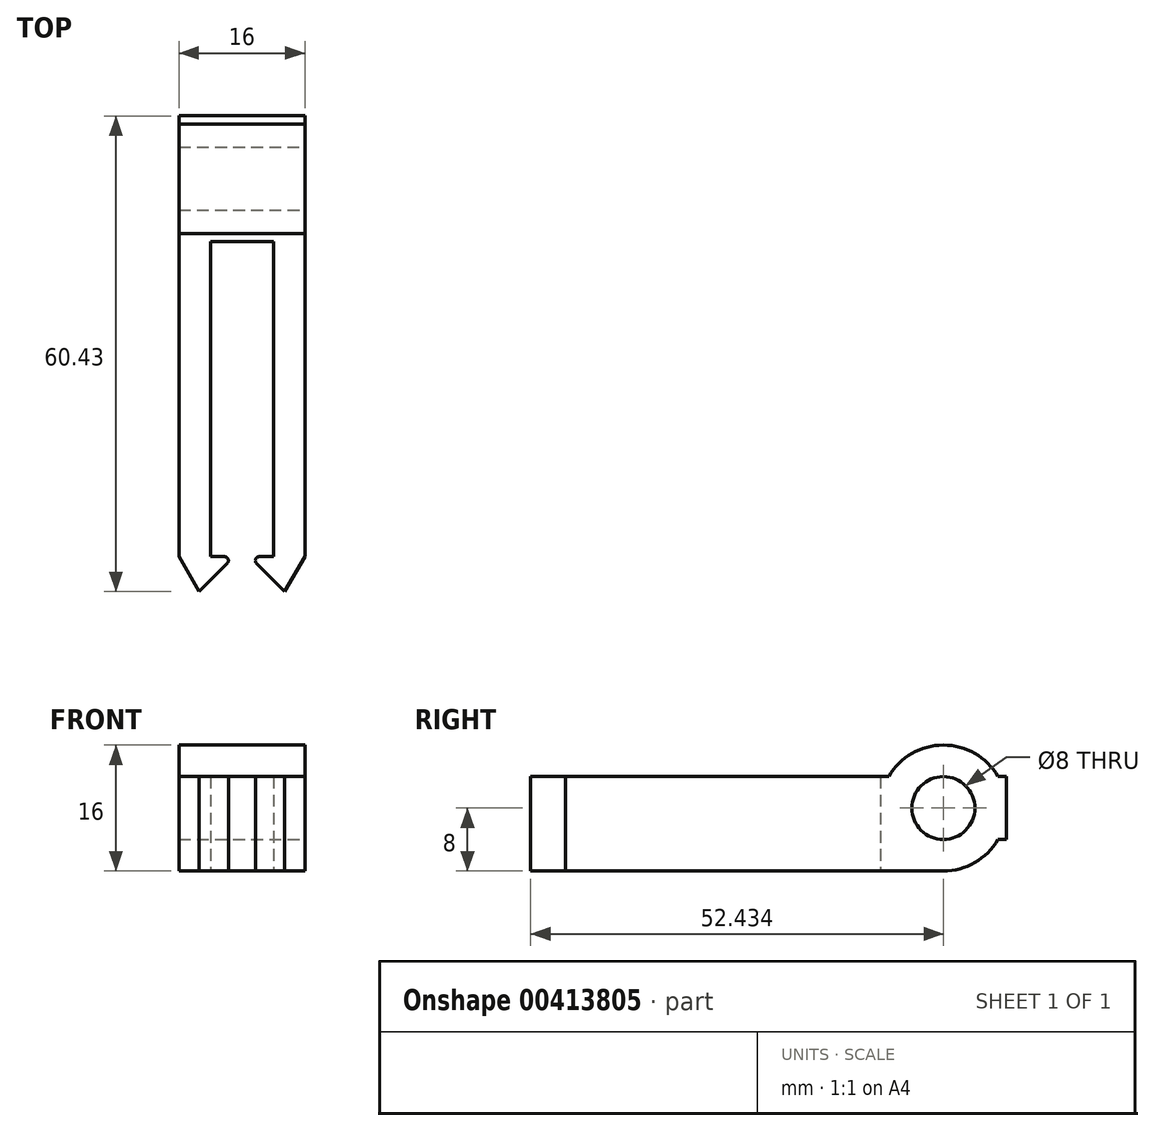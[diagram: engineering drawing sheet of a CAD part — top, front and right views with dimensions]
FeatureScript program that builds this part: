
annotation { "Feature Type Name" : "Feature", "Feature Type Description" : "" }
export const myFeature = defineFeature(function(context is Context, id is Id, definition is map)
    precondition{}
    {
        {
            var Q0;
            Q0=qCreatedBy(makeId("Top.planeOp"),FACE);
            var sketch = newSketch(context, id + "F0", { "sketchPlane" : qUnion([Q0])});
            skLineSegment(sketch, "E0", {"start": v(12.47, 0) * mm, "end": v(9.92, 4.43) * mm});
            skLineSegment(sketch, "E1", {"start": v(12.47, 0) * mm, "end": v(16.07, 3.58) * mm});
            skLineSegment(sketch, "E2", {"start": v(15.71, 4.43) * mm, "end": v(13.92, 4.43) * mm});
            skLineSegment(sketch, "E3", {"start": v(13.92, 4.43) * mm, "end": v(13.92, 44.43) * mm});
            skLineSegment(sketch, "E4", {"start": v(9.92, 4.43) * mm, "end": v(9.92, 44.43) * mm});
            skLineSegment(sketch, "E5", {"start": v(17.92, 4.43) * mm, "end": v(17.92, 23.26) * mm, "construction": true});
            skPoint(sketch, "E6.visualSharp", {"position": v(16.92, 4.43) * mm});
            skArc(sketch, "E6.filletArc", {"start": v(16.07, 3.58) * mm, "mid": v(16.18, 4.13) * mm, "end": v(15.71, 4.43) * mm});
            skLineSegment(sketch, "E7.MirrorCS", {"start": v(21.92, 4.43) * mm, "end": v(21.92, 44.43) * mm});
            skLineSegment(sketch, "E8.MirrorCS", {"start": v(20.13, 4.43) * mm, "end": v(21.92, 4.43) * mm});
            skLineSegment(sketch, "E9.MirrorCS", {"start": v(23.37, 0) * mm, "end": v(19.78, 3.58) * mm});
            skLineSegment(sketch, "E10.MirrorCS", {"start": v(23.37, 0) * mm, "end": v(25.92, 4.43) * mm});
            skLineSegment(sketch, "E11.MirrorCS", {"start": v(25.92, 4.43) * mm, "end": v(25.92, 44.43) * mm});
            skArc(sketch, "E12.MirrorCS", {"start": v(19.78, 3.58) * mm, "mid": v(19.67, 4.13) * mm, "end": v(20.13, 4.43) * mm});
            skLineSegment(sketch, "E13.bottom", {"start": v(25.92, 44.43) * mm, "end": v(9.92, 44.43) * mm});
            skLineSegment(sketch, "E13.top", {"start": v(25.92, 60.43) * mm, "end": v(9.92, 60.43) * mm});
            skLineSegment(sketch, "E13.left", {"start": v(25.92, 44.43) * mm, "end": v(25.92, 60.43) * mm});
            skLineSegment(sketch, "E13.right", {"start": v(9.92, 44.43) * mm, "end": v(9.92, 60.43) * mm});
            skSolve(sketch);
        }
        {
            var Q0;
            Q0=makeQuery(id+"F0.imprint","IMPRINT",FACE,{"disambiguationData":[TD([[makeQuery(id+"F0.imprint","IMPRINT",EDGE,{"derivedFrom":sQuery(id+"F0.wireOp",EDGE,"E13.top")}),1.0]])]});
            var Q1;
            {var subQ1=sQuery(id+"F0.wireOp",EDGE,"E0");Q1=makeQuery(id+"F0.imprint","IMPRINT",FACE,{"disambiguationData":[TD([[makeQuery(id+"F0.imprint","IMPRINT",EDGE,{"derivedFrom":subQ1}),-1.0]])]});}
            var Q2;
            {var subQ1=sQuery(id+"F0.wireOp",EDGE,"E7.MirrorCS");Q2=makeQuery(id+"F0.imprint","IMPRINT",FACE,{"disambiguationData":[TD([[makeQuery(id+"F0.imprint","IMPRINT",EDGE,{"derivedFrom":subQ1}),-1.0]])]});}
            extrude(context, id + "F1", {"entities" : qUnion([Q0, Q1, Q2]), "endBound" : BoundingType.SYMMETRIC, "depth" : 8 * mm});
        }
        {
            var Q0;
            Q0=makeQuery(id+"F1.opExtrude","SWEPT_FACE",FACE,{"disambiguationData":[OSD([sQuery(id+"F0.wireOp",EDGE,"E11.MirrorCS"),sQuery(id+"F0.wireOp",EDGE,"E13.left")])]});
            var sketch = newSketch(context, id + "F2", { "sketchPlane" : qUnion([Q0])});
            skCircle(sketch, "E14", {"center": v(52.43, 0) * mm, "radius": 4 * mm});
            skCircle(sketch, "E15.0", {"center": v(52.43, 0) * mm, "radius": 8 * mm});
            skPoint(sketch, "E16", {"position": v(44.43, 0) * mm});
            skPoint(sketch, "E17", {"position": v(52.43, -8) * mm});
            skLineSegment(sketch, "E18", {"start": v(0, -8) * mm, "end": v(0, -4) * mm});
            skLineSegment(sketch, "E19", {"start": v(0, -4) * mm, "end": v(45.5, -4) * mm});
            skLineSegment(sketch, "E20", {"start": v(52.43, -8) * mm, "end": v(0, -8) * mm});
            skSolve(sketch);
        }
        {
            var Q0;
            {var subQ0=sQuery(id+"F2.wireOp",EDGE,"E15.0");var subQ1=makeQuery(id+"F2.imprint","INTERSECT",VERTEX,{"derivedFrom":[subQ0,sQuery(id+"F2.wireOp",EDGE,"E20")]});Q0=makeQuery(id+"F2.imprint","IMPRINT",FACE,{"disambiguationData":[TD([[makeQuery(id+"F2.imprint","IMPRINT",EDGE,{"disambiguationData":[TD([[subQ1,-1.0]])],"derivedFrom":subQ0}),1.0]])]});}
            var Q1;
            {var subQ5=sQuery(id+"F2.wireOp",EDGE,"E18");Q1=makeQuery(id+"F2.imprint","IMPRINT",FACE,{"disambiguationData":[TD([[makeQuery(id+"F2.imprint","IMPRINT",EDGE,{"derivedFrom":subQ5}),-1.0]])]});}
            var Q2;
            {var subQ0=sQuery(id+"F2.wireOp",EDGE,"E15.0");var subQ1=makeQuery(id+"F1.opExtrude","CAP_EDGE",EDGE,{"disambiguationData":[OSD([sQuery(id+"F0.wireOp",EDGE,"E11.MirrorCS"),sQuery(id+"F0.wireOp",EDGE,"E13.left")])],"isStart":false});var subQ2=makeQuery(id+"F2.imprint","INTERSECT",VERTEX,{"disambiguationData":[OD(0.0)],"derivedFrom":[subQ1,subQ0]});Q2=makeQuery(id+"F2.imprint","IMPRINT",FACE,{"disambiguationData":[TD([[makeQuery(id+"F2.imprint","IMPRINT",EDGE,{"disambiguationData":[TD([[subQ2,-1.0]])],"derivedFrom":subQ0}),1.0]])]});}
            var Q3;
            Q3=makeQuery(id+"F1.opExtrude","SWEPT_FACE",FACE,{"disambiguationData":[OSD([sQuery(id+"F0.wireOp",EDGE,"E4"),sQuery(id+"F0.wireOp",EDGE,"E13.right")])]});
            extrude(context, id + "F3", {"entities" : qUnion([Q0, Q1, Q2]), "operationType" : NewBodyOperationType.ADD, "endBound" : BoundingType.UP_TO_SURFACE, "oppositeDirection" : true, "endBoundEntityFace" : qUnion([Q3]), "depth" : 25 * mm});
        }
        {
            var Q0;
            {var subQ0=sQuery(id+"F2.wireOp",EDGE,"E14");var subQ1=sQuery(id+"F0.wireOp",EDGE,"E13.left");var subQ2=sQuery(id+"F0.wireOp",EDGE,"E11.MirrorCS");var subQ3=makeQuery(id+"F2.imprint","INTERSECT",VERTEX,{"derivedFrom":[makeQuery(id+"F1.opExtrude","CAP_EDGE",EDGE,{"disambiguationData":[OSD([subQ2,subQ1])],"isStart":false}),subQ0]});Q0=makeQuery(id+"F2.imprint","IMPRINT",FACE,{"disambiguationData":[TD([[makeQuery(id+"F2.imprint","IMPRINT",EDGE,{"disambiguationData":[TD([[subQ3,-1.0]])],"derivedFrom":subQ0}),1.0]])]});}
            extrude(context, id + "F4", {"entities" : qUnion([Q0]), "operationType" : NewBodyOperationType.REMOVE, "oppositeDirection" : true, "depth" : 25 * mm});
        }
        {
            var Q0;
            {var subQ0=makeQuery(id+"F3.opExtrude","SWEPT_FACE",FACE,{"disambiguationData":[OSD([sQuery(id+"F0.wireOp",EDGE,"E11.MirrorCS"),sQuery(id+"F0.wireOp",EDGE,"E13.left"),sQuery(id+"F2.wireOp",EDGE,"E19")])]});Q0=makeQuery(id+"F3.boolean.opBoolean","SPLIT",FACE,{"disambiguationData":[TD([makeQuery(id+"F1.opExtrude","SWEPT_FACE",FACE,{"disambiguationData":[OSD([sQuery(id+"F0.wireOp",EDGE,"E2")])]})])],"derivedFrom":subQ0});}
            var Q1;
            {var subQ0=sQuery(id+"F0.wireOp",EDGE,"E13.right");var subQ1=sQuery(id+"F0.wireOp",EDGE,"E4");var subQ2=sQuery(id+"F0.wireOp",EDGE,"E13.left");var subQ3=sQuery(id+"F0.wireOp",EDGE,"E11.MirrorCS");var subQ4=makeQuery(id+"F3.opExtrude","SWEPT_FACE",FACE,{"disambiguationData":[OSD([subQ3,subQ2,sQuery(id+"F2.wireOp",EDGE,"E19")])]});Q1=makeQuery(id+"F3.boolean.opBoolean","SPLIT",FACE,{"disambiguationData":[TD([makeQuery(id+"F1.opExtrude","SWEPT_FACE",FACE,{"disambiguationData":[OSD([subQ1,subQ0])]})])],"derivedFrom":subQ4});}
            var Q2;
            {var subQ1=sQuery(id+"F0.wireOp",EDGE,"E13.left");var subQ2=sQuery(id+"F0.wireOp",EDGE,"E11.MirrorCS");var subQ3=sQuery(id+"F2.wireOp",EDGE,"E19");var subQ5=makeQuery(id+"F3.opExtrude","SWEPT_FACE",FACE,{"disambiguationData":[OSD([subQ2,subQ1,subQ3])]});Q2=makeQuery(id+"F3.boolean.opBoolean","SPLIT",FACE,{"disambiguationData":[TD([makeQuery(id+"F1.opExtrude","SWEPT_FACE",FACE,{"disambiguationData":[OSD([subQ2,subQ1])]})])],"derivedFrom":subQ5});}
            extrude(context, id + "F5", {"entities" : qUnion([Q0, Q1, Q2]), "operationType" : NewBodyOperationType.REMOVE, "oppositeDirection" : true, "depth" : 25 * mm});
        }
    });
